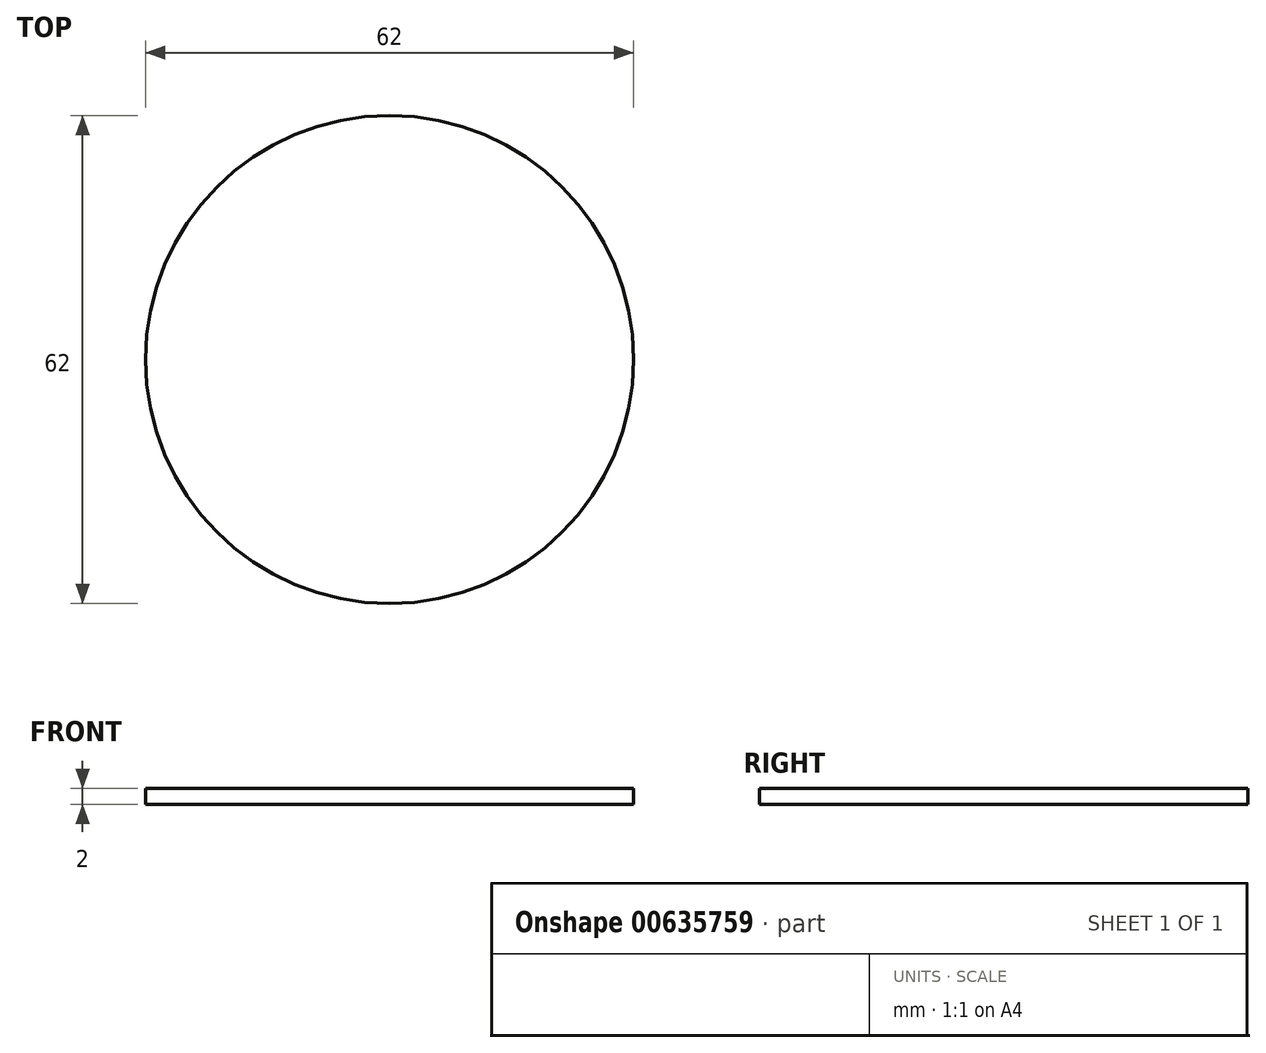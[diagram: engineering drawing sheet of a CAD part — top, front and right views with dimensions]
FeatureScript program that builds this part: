
annotation { "Feature Type Name" : "Feature", "Feature Type Description" : "" }
export const myFeature = defineFeature(function(context is Context, id is Id, definition is map)
    precondition{}
    {
        {
            var Q0;
            Q0=qCreatedBy(makeId("Top.planeOp"),FACE);
            var sketch = newSketch(context, id + "F0", { "sketchPlane" : qUnion([Q0])});
            skCircle(sketch, "E0", {"center": v(0, 0) * mm, "radius": 31 * mm});
            skSolve(sketch);
        }
        {
            var Q0;
            Q0=makeQuery(id+"F0.imprint","IMPRINT",FACE,{"disambiguationData":[TD([[makeQuery(id+"F0.imprint","IMPRINT",EDGE,{"derivedFrom":sQuery(id+"F0.wireOp",EDGE,"E0")}),1.0]])]});
            extrude(context, id + "F1", {"entities" : qUnion([Q0]), "depth" : 2 * mm, "offsetDistance" : 25 * mm});
        }
        {
            var Q0;
            Q0=makeQuery(id+"F1.opExtrude","CAP_FACE",FACE,{"disambiguationData":[OSD([sQuery(id+"F0.wireOp",EDGE,"E0")])],"isStart":false});
            var sketch = newSketch(context, id + "F2", { "sketchPlane" : qUnion([Q0])});
            skText(sketch, "E1", { "text": "1\n", "fontName": "OpenSans-Regular.ttf"});
            const initialGuessF2  = {"E1": [-0.01711, -0.01987, 1, 0, 0.03882]};
            skSetInitialGuess(sketch, initialGuessF2);
            skSolve(sketch);
        }
        {
            var Q0;
            Q0 = qConstructionFilter(qBodyType(qCreatedBy(id + "F2" ,EDGE), BodyType.WIRE), ConstructionObject.NO);
            extrude(context, id + "F3", {"bodyType" : ToolBodyType.SURFACE, "surfaceEntities" : qUnion([Q0]), "depth" : 2 * mm, "offsetDistance" : 25 * mm});
        }
    });
